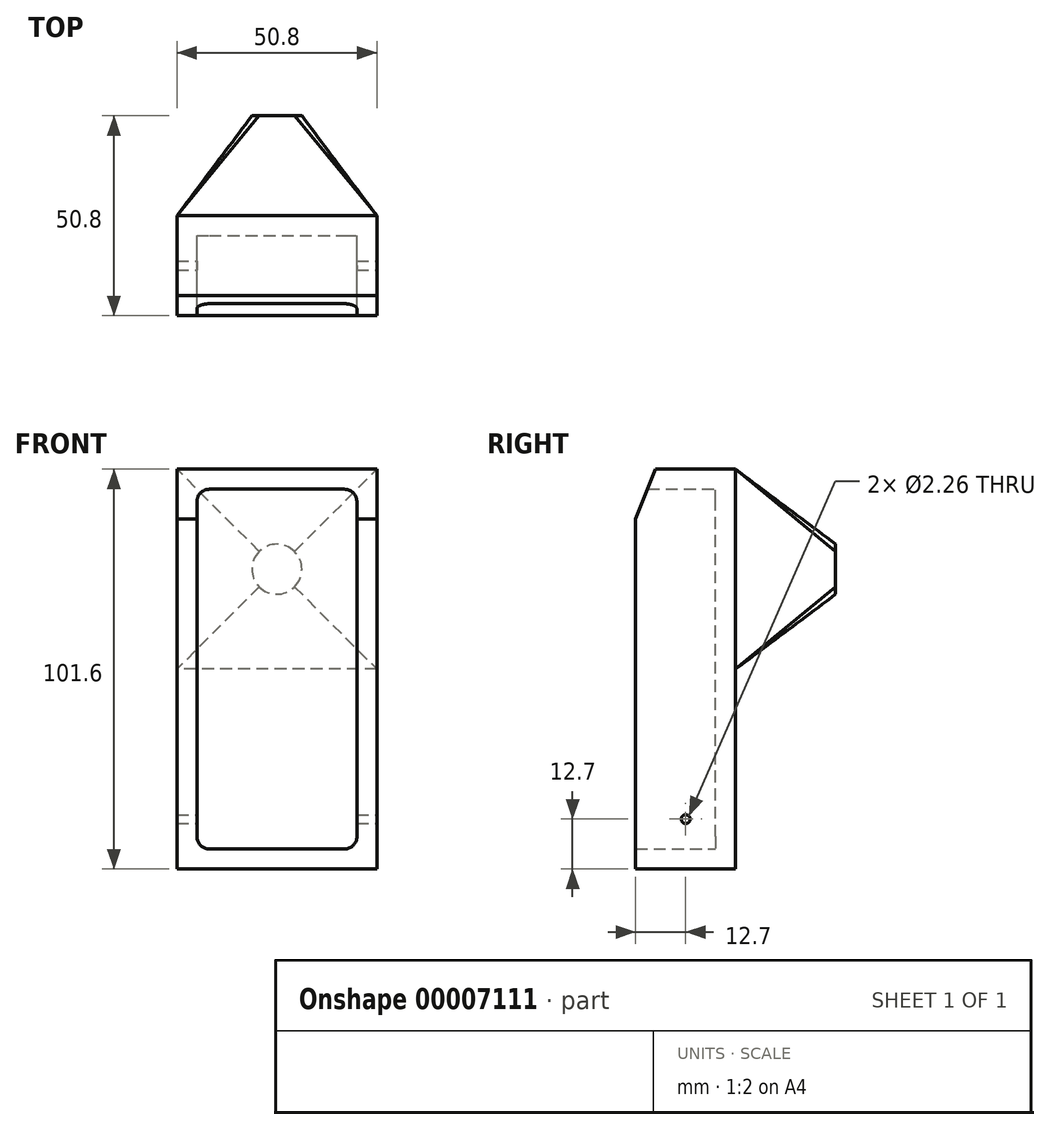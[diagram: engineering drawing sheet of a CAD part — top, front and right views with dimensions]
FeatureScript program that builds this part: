
annotation { "Feature Type Name" : "Feature", "Feature Type Description" : "" }
export const myFeature = defineFeature(function(context is Context, id is Id, definition is map)
    precondition{}
    {
        {
            var Q0;
            Q0=qCreatedBy(makeId("Front.planeOp"),FACE);
            var sketch = newSketch(context, id + "F0", { "sketchPlane" : qUnion([Q0])});
            skLineSegment(sketch, "E0.bottom", {"start": v(0, 0) * mm, "end": v(50.8, 0) * mm});
            skLineSegment(sketch, "E0.top", {"start": v(0, 101.6) * mm, "end": v(50.8, 101.6) * mm});
            skLineSegment(sketch, "E0.left", {"start": v(0, 0) * mm, "end": v(0, 101.6) * mm});
            skLineSegment(sketch, "E0.right", {"start": v(50.8, 0) * mm, "end": v(50.8, 101.6) * mm});
            skSolve(sketch);
        }
        {
            var Q0;
            Q0 = qSketchRegion(id + "F0", true);
            extrude(context, id + "F1", {"entities" : qUnion([Q0]), "depth" : 25.4 * mm});
        }
        {
            var Q0;
            Q0=makeQuery(id+"F1.opExtrude","CAP_EDGE",EDGE,{"disambiguationData":[OSD([sQuery(id+"F0.wireOp",EDGE,"E0.top")])],"isStart":false});
            chamfer(context, id + "F2", {"entities" : qUnion([Q0]), "chamferType" : ChamferType.TWO_OFFSETS, "width1" : 5.08 * mm, "oppositeDirection" : false, "width2" : 12.7 * mm, "tangentPropagation" : true});
        }
        {
            var Q0;
            Q0=makeQuery(id+"F1.opExtrude","CAP_FACE",FACE,{"disambiguationData":[OSD([sQuery(id+"F0.wireOp",EDGE,"E0.bottom"),sQuery(id+"F0.wireOp",EDGE,"E0.top"),sQuery(id+"F0.wireOp",EDGE,"E0.left"),sQuery(id+"F0.wireOp",EDGE,"E0.right")])],"isStart":false});
            var Q1;
            Q1=makeQuery(id+"F2.opChamfer","BLEND_FACE",FACE,{"disambiguationData":[OSD([sQuery(id+"F0.wireOp",EDGE,"E0.top")])]});
            shell(context, id + "F3", {"entities" : qUnion([Q0, Q1]), "thickness" : 5.08 * mm});
        }
        {
            var Q0;
            {var subQ0=sQuery(id+"F0.wireOp",EDGE,"E0.left");var subQ1=sQuery(id+"F0.wireOp",EDGE,"E0.top");Q0=makeQuery(id+"F3.opShell","OFFSET_EDGE",EDGE,{"disambiguationData":[OSD([subQ1,subQ0]),TDD([makeQuery(id+"F1.opExtrude","SWEPT_EDGE",EDGE,{"disambiguationData":[OSD([subQ1,subQ0])]})])]});}
            var Q1;
            {var subQ0=sQuery(id+"F0.wireOp",EDGE,"E0.right");var subQ1=sQuery(id+"F0.wireOp",EDGE,"E0.top");Q1=makeQuery(id+"F3.opShell","OFFSET_EDGE",EDGE,{"disambiguationData":[OSD([subQ1,subQ0]),TDD([makeQuery(id+"F1.opExtrude","SWEPT_EDGE",EDGE,{"disambiguationData":[OSD([subQ1,subQ0])]})])]});}
            var Q2;
            Q2=makeQuery(id+"F3.opShell","OFFSET_EDGE",EDGE,{"disambiguationData":[OSD([sQuery(id+"F0.wireOp",EDGE,"E0.bottom"),sQuery(id+"F0.wireOp",EDGE,"E0.right")])]});
            var Q3;
            Q3=makeQuery(id+"F3.opShell","OFFSET_EDGE",EDGE,{"disambiguationData":[OSD([sQuery(id+"F0.wireOp",EDGE,"E0.bottom"),sQuery(id+"F0.wireOp",EDGE,"E0.left")])]});
            fillet(context, id + "F4", {"entities" : qUnion([Q0, Q1, Q2, Q3]), "radius" : 3.17 * mm, "tangentPropagation" : true, "allowEdgeOverflow" : false});
        }
        {
            var Q0;
            Q0=makeQuery(id+"F1.opExtrude","SWEPT_FACE",FACE,{"disambiguationData":[OSD([sQuery(id+"F0.wireOp",EDGE,"E0.right")])]});
            var sketch = newSketch(context, id + "F5", { "sketchPlane" : qUnion([Q0])});
            skPoint(sketch, "E1", {"position": v(-12.7, 12.7) * mm});
            skSolve(sketch);
        }
        {
            var Q0;
            Q0=sQuery(id+"F5.wireOp",VERTEX,"E1");
            var Q1;
            Q1=makeQuery(id+"F1.opExtrude","SWEPT_BODY",BODY,{"disambiguationData":[OSD([sQuery(id+"F0.wireOp",EDGE,"E0.bottom"),sQuery(id+"F0.wireOp",EDGE,"E0.top"),sQuery(id+"F0.wireOp",EDGE,"E0.left"),sQuery(id+"F0.wireOp",EDGE,"E0.right")])]});
            hole(context, id + "F6", {"style" : HoleStyle.SIMPLE, "endStyle" : HoleEndStyle.THROUGH, "standardTappedOrClearance" : lookupTablePath({ "standard" : "ANSI", "engagement" : "75%", "pitch" : "40 tpi", "size" : "#4", "type" : "Tapped" }), "standardBlindInLast" : lookupTablePath({ "standard" : "ANSI", "engagement" : "75%", "pitch" : "40 tpi", "size" : "#4", "type" : "Tapped" }), "holeDiameter" : 2.26 * mm, "locations" : qUnion([Q0]), "scope" : qUnion([Q1]), "isTappedThrough" : true, "majorDiameter" : 2.84 * mm, "showTappedDepth" : true});
        }
        {
            var Q0;
            Q0=makeQuery(id+"F0.imprint","IMPRINT",FACE,{"disambiguationData":[TD([[makeQuery(id+"F0.imprint","IMPRINT",EDGE,{"derivedFrom":sQuery(id+"F0.wireOp",EDGE,"E0.bottom")}),1.0]])]});
            cPlane(context, id + "F7", {"entities" : qUnion([Q0]), "cplaneType" : CPlaneType.OFFSET, "offset" : 25.4 * mm, "oppositeDirection" : true, "width" : 152.4 * mm, "height" : 152.4 * mm});
        }
        {
            var Q0;
            Q0=qCreatedBy(id+"F7.planeOp",FACE);
            var sketch = newSketch(context, id + "F8", { "sketchPlane" : qUnion([Q0])});
            skCircle(sketch, "E2", {"center": v(25.4, 76.2) * mm, "radius": 6.35 * mm});
            skSolve(sketch);
        }
        {
            var Q0;
            Q0=makeQuery(id+"F0.imprint","IMPRINT",FACE,{"disambiguationData":[TD([[makeQuery(id+"F0.imprint","IMPRINT",EDGE,{"derivedFrom":sQuery(id+"F0.wireOp",EDGE,"E0.bottom")}),1.0]])]});
            var sketch = newSketch(context, id + "F9", { "sketchPlane" : qUnion([Q0])});
            skLineSegment(sketch, "E3.bottom", {"start": v(50.8, 101.6) * mm, "end": v(0, 101.6) * mm});
            skLineSegment(sketch, "E3.top", {"start": v(50.8, 50.8) * mm, "end": v(0, 50.8) * mm});
            skLineSegment(sketch, "E3.left", {"start": v(50.8, 101.6) * mm, "end": v(50.8, 50.8) * mm});
            skLineSegment(sketch, "E3.right", {"start": v(0, 101.6) * mm, "end": v(0, 50.8) * mm});
            skSolve(sketch);
        }
        {
            var Q1;
            Q1 = qSketchRegion(id + "F8", true);
            var Q2;
            Q2 = qSketchRegion(id + "F9", true);
            loft(context, id + "F10", {"operationType" : NewBodyOperationType.ADD, "sheetProfilesArray" : [{ "sheetProfileEntities" : qUnion([Q1]) }, { "sheetProfileEntities" : qUnion([Q2]) }]});
        }
    });
